# Revit family: Hager-Univers-IP43-D349-H898-Cl.II-Fire_res.encl_30min-NoHosted-CH-it
name_source: partatom
category: Electrical Equipment
units: mm (PartAtom-declared; Revit-internal decimal feet)

## family parameters
Always vertical = Yes
Cut with Voids When Loaded = No
Panel Configuration = Two Columns, Circuits Across
Part Type = Panelboard
Room Calculation Point = No
Round Connector Dimension = Use Diameter
Shared = No
Work Plane-Based = Yes

## types (2) — shared parameters
Default Elevation = 1219 mm
EF000003 - Tipo di montaggio = EV000384 - A parete
EF000007 - colore = EV000270 - grigio
EF000040 - Altezza = 898 mm  [stored 2.94619 ft]
EF000049 - profondità = 349 mm  [stored 1.14501 ft]
EF000116 - numero RAL = 7035
EF000118 - con piastra di montaggio = No
EF000266 - numero di file = 5
EF000339 - tipo di copertura = EV004216 - porta
EF001088 - possibilità di applicazione = No
EF001131 - profondità interna = 240 mm  [stored 0.787402 ft]
EF001596 - Attacco Lampada = EV000139 - plastica
EF001613 - Integrità del circuito = EV004178 - E 30
EF003532 - adatto per uso esterno = No
EF004293 - resistenza agli urti = EV008784 - IK10
EF004464 - tipo di porta = EV002646 - singolo
EF005474 - grado di protezione (IP) = EV006610 - IP43
EF006244 - coperchio/porta trasparente = No
EF006306 - con serratura = Yes
EF007800 - adatto per parafulmine = No
EF008873 - corrente nominale (In) = 250 A
EF009170 - spessore materiale scatola = 70 mm  [stored 0.229659 ft]
EF009171 - spessore materiale porta/coperchio = 22 mm  [stored 0.0721785 ft]
EF009212 - esecuzione coperchio = EV000116 - chiuso
EF015940 - Coprire con rilascio di sovrapressione = No
HG000002 - Con porta = Yes
HG000003 - Gamma = Univers
HG000006 - Ad incasso = No
HG000009 - Porta doppia a battente = No
HG000010 - Porte asimmetriche = No
HG000023 - Custodia a doppia sezione = No
HG000024 - Altezza della sezione inferiore = 600 mm
HG000026 - A pavimento = No
Manufacturer = Hager
Type Comments = Univers
zero-valued in all types: EF000218 - profondità di incasso, HG000027 - Altezza dello zoccolo

## per-type parameters (varying)
| type | EF000008 - Larghezza | EF000437 - numero di ingressi per conduttori | EF002950 - Numero moduli DIN | EF004427 - numero di moduli | EF009554 - numero delle aperture per la piastra della flangia | HG000004 - Codice produttore |
| A parete IP43 L398 A898 P349  - FB51LE | 398 mm  [stored 1.30577 ft] | 1 | 12 | 60 | 2 | FB51LE |
| A parete IP43 L648 A898 P349  - FB52LE | 648 mm  [stored 2.12598 ft] | 2 | 24 | 120 | 4 | FB52LE |

note: [stored X ft] marks values corroborated as IEEE doubles in the binary element streams (Revit-internal decimal feet)

## geometry (parser evidence)
native form markers: Blend x4, Sweep x5
no freeform markers — native parametric forms only
